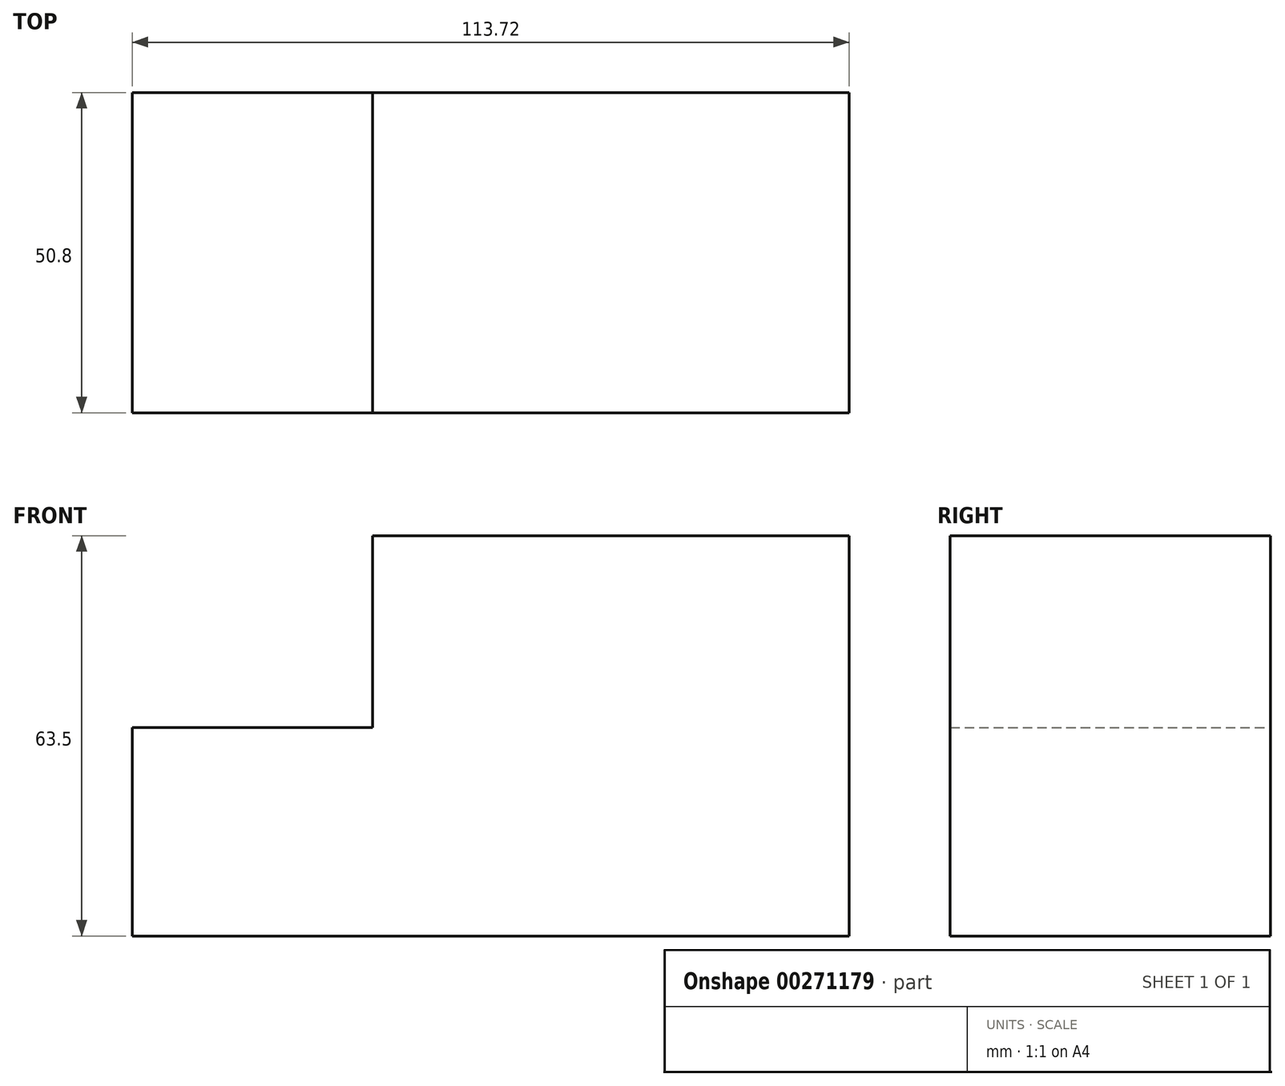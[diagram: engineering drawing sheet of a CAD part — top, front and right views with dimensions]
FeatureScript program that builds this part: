
annotation { "Feature Type Name" : "Feature", "Feature Type Description" : "" }
export const myFeature = defineFeature(function(context is Context, id is Id, definition is map)
    precondition{}
    {
        {
            var Q0;
            Q0=qCreatedBy(makeId("Front.planeOp"),FACE);
            var sketch = newSketch(context, id + "F0", { "sketchPlane" : qUnion([Q0])});
            skLineSegment(sketch, "E0.bottom", {"start": v(0, 0) * mm, "end": v(75.62, 0) * mm});
            skLineSegment(sketch, "E0.top", {"start": v(0, 63.5) * mm, "end": v(75.62, 63.5) * mm});
            skLineSegment(sketch, "E0.left", {"start": v(0, 0) * mm, "end": v(0, 63.5) * mm});
            skLineSegment(sketch, "E0.right", {"start": v(75.62, 0) * mm, "end": v(75.62, 63.5) * mm});
            skLineSegment(sketch, "E1.bottom", {"start": v(0, 0) * mm, "end": v(-38.1, 0) * mm});
            skLineSegment(sketch, "E1.top", {"start": v(0, 33.04) * mm, "end": v(-38.1, 33.04) * mm});
            skLineSegment(sketch, "E1.left", {"start": v(0, 0) * mm, "end": v(0, 33.04) * mm});
            skLineSegment(sketch, "E1.right", {"start": v(-38.1, 0) * mm, "end": v(-38.1, 33.04) * mm});
            skSolve(sketch);
        }
        {
            var Q0;
            Q0 = qSketchRegion(id + "F0", true);
            extrude(context, id + "F1", {"entities" : qUnion([Q0]), "depth" : 50.8 * mm});
        }
    });
